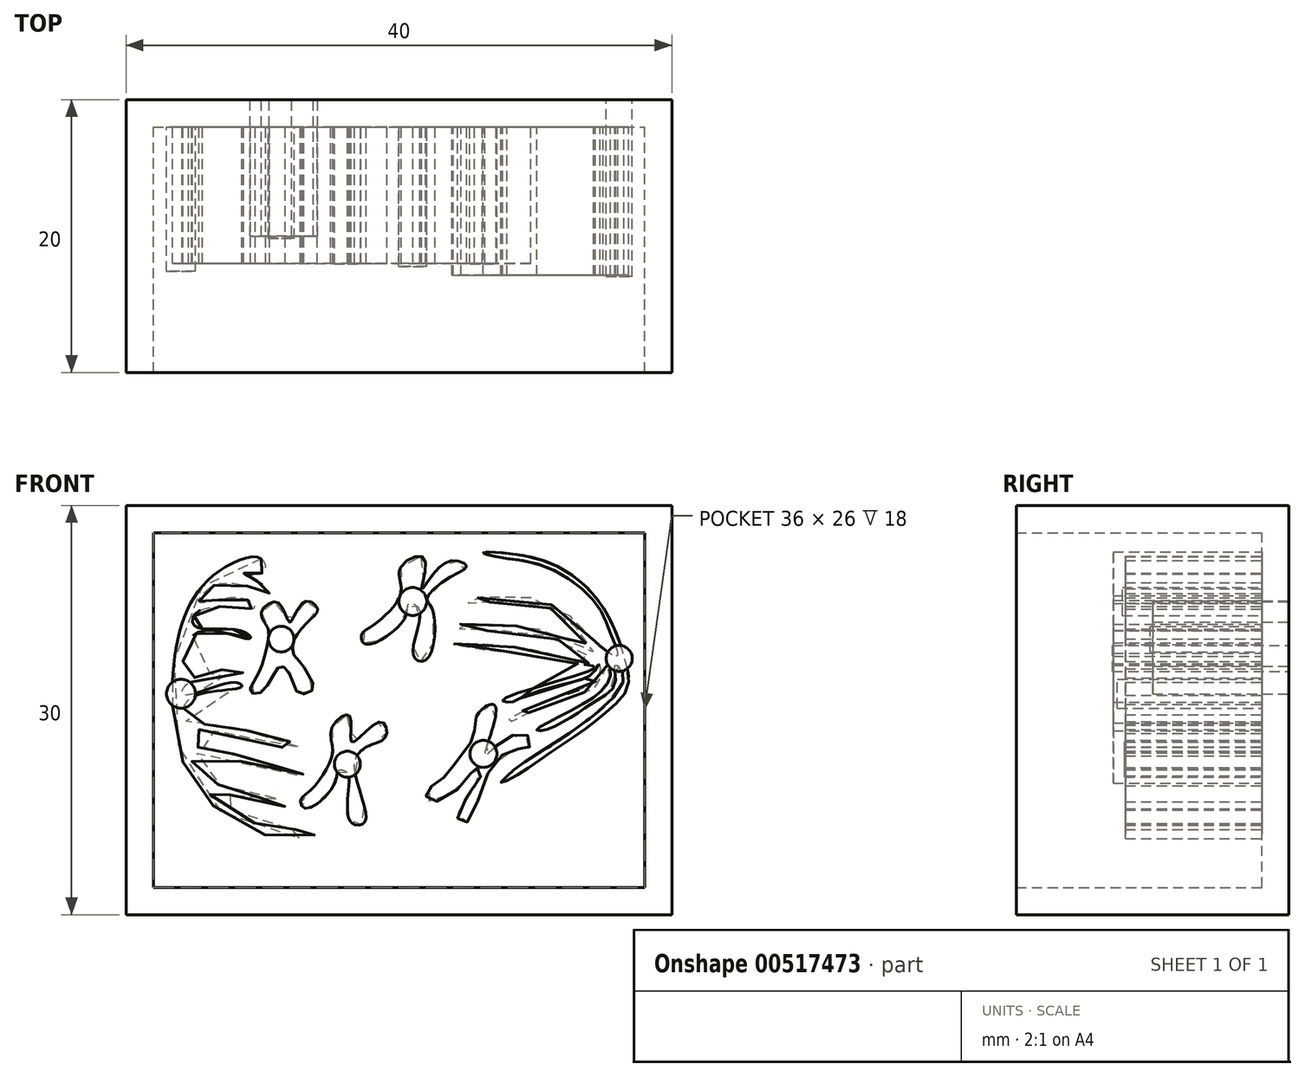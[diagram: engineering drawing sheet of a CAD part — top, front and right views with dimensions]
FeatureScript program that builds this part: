
annotation { "Feature Type Name" : "Feature", "Feature Type Description" : "" }
export const myFeature = defineFeature(function(context is Context, id is Id, definition is map)
    precondition{}
    {
        {
            var Q0;
            Q0=qCreatedBy(makeId("Front.planeOp"),FACE);
            var sketch = newSketch(context, id + "F0", { "sketchPlane" : qUnion([Q0])});
            skLineSegment(sketch, "E0.bottom", {"start": v(0, 0) * mm, "end": v(40, 0) * mm});
            skLineSegment(sketch, "E0.top", {"start": v(0, 30) * mm, "end": v(40, 30) * mm});
            skLineSegment(sketch, "E0.left", {"start": v(0, 0) * mm, "end": v(0, 30) * mm});
            skLineSegment(sketch, "E0.right", {"start": v(40, 0) * mm, "end": v(40, 30) * mm});
            skSolve(sketch);
        }
        {
            var Q0;
            Q0 = qSketchRegion(id + "F0", true);
            extrude(context, id + "F1", {"entities" : qUnion([Q0]), "depth" : 20 * mm, "offsetDistance" : 25 * mm});
        }
        {
            var Q0;
            Q0=makeQuery(id+"F1.opExtrude","CAP_FACE",FACE,{"disambiguationData":[OSD([sQuery(id+"F0.wireOp",EDGE,"E0.bottom"),sQuery(id+"F0.wireOp",EDGE,"E0.top"),sQuery(id+"F0.wireOp",EDGE,"E0.left"),sQuery(id+"F0.wireOp",EDGE,"E0.right")])],"isStart":false});
            shell(context, id + "F2", {"entities" : qUnion([Q0]), "thickness" : 2 * mm});
        }
        {
            var Q0;
            Q0=qCreatedBy(makeId("Front.planeOp"),FACE);
            var sketch = newSketch(context, id + "F3", { "sketchPlane" : qUnion([Q0])});
            skFitSpline(sketch, "E1", {"points": [v(9.93, 22.19) * mm, v(10.4, 20.93) * mm, v(10.3, 19.64) * mm, v(10.05, 18.55) * mm, v(9.52, 17.35) * mm, v(9.1, 16.41) * mm, v(9.73, 16.2) * mm, v(10.77, 17.52) * mm, v(11.37, 18.2) * mm, v(12.06, 17.5) * mm, v(12.66, 16.23) * mm, v(13.69, 16.52) * mm, v(13.32, 17.66) * mm, v(12.78, 18.46) * mm, v(12.14, 19.45) * mm, v(13.27, 21.42) * mm, v(14.04, 22.42) * mm, v(13.07, 22.95) * mm, v(11.98, 21.44) * mm, v(11.15, 22.87) * mm, v(9.93, 22.19) * mm]});
            skSolve(sketch);
        }
        {
            var Q0;
            Q0 = qSketchRegion(id + "F3", true);
            extrude(context, id + "F4", {"entities" : qUnion([Q0]), "depth" : 10 * mm, "offsetDistance" : 25 * mm});
        }
        {
            var Q0;
            Q0=makeQuery(id+"F2.opShell","OFFSET_FACE",FACE,{"disambiguationData":[OSD([sQuery(id+"F0.wireOp",EDGE,"E0.bottom"),sQuery(id+"F0.wireOp",EDGE,"E0.top"),sQuery(id+"F0.wireOp",EDGE,"E0.left"),sQuery(id+"F0.wireOp",EDGE,"E0.right")])]});
            var sketch = newSketch(context, id + "F5", { "sketchPlane" : qUnion([Q0])});
            skFitSpline(sketch, "E2", {"points": [v(15.1, 13.72) * mm, v(15.16, 12.14) * mm, v(14.66, 10.62) * mm, v(13.54, 9.13) * mm, v(12.78, 8.35) * mm, v(13.2, 7.78) * mm, v(15.3, 9.65) * mm, v(15.56, 10.57) * mm, v(16.2, 10.4) * mm, v(16.28, 8.97) * mm, v(16.23, 7.64) * mm, v(16.56, 6.7) * mm, v(17.53, 6.83) * mm, v(16.74, 10.92) * mm, v(17.86, 12.42) * mm, v(19.08, 13.14) * mm, v(18.62, 14.14) * mm, v(16.55, 12.66) * mm, v(16.38, 14.58) * mm, v(15.1, 13.72) * mm]});
            skSolve(sketch);
        }
        {
            var Q0;
            Q0 = qSketchRegion(id + "F5", true);
            extrude(context, id + "F6", {"entities" : qUnion([Q0]), "depth" : 10 * mm, "offsetDistance" : 25 * mm});
        }
        {
            var Q0;
            Q0=makeQuery(id+"F2.opShell","OFFSET_FACE",FACE,{"disambiguationData":[OSD([sQuery(id+"F0.wireOp",EDGE,"E0.bottom"),sQuery(id+"F0.wireOp",EDGE,"E0.top"),sQuery(id+"F0.wireOp",EDGE,"E0.left"),sQuery(id+"F0.wireOp",EDGE,"E0.right")])]});
            var sketch = newSketch(context, id + "F7", { "sketchPlane" : qUnion([Q0])});
            skFitSpline(sketch, "E3", {"points": [v(20.14, 25.5) * mm, v(20.17, 23.8) * mm, v(19.24, 22.18) * mm, v(17.97, 21.13) * mm, v(17.25, 20.52) * mm, v(17.49, 19.86) * mm, v(19.1, 20.42) * mm, v(20.57, 22.07) * mm, v(20.73, 22.8) * mm, v(21.4, 22.51) * mm, v(21.33, 20.84) * mm, v(21.16, 18.8) * mm, v(22.12, 18.8) * mm, v(22.4, 22.5) * mm, v(22.03, 23.13) * mm, v(23.72, 24.74) * mm, v(24.95, 25.56) * mm, v(24.15, 25.97) * mm, v(22.57, 25.06) * mm, v(21.67, 23.9) * mm, v(21.83, 26.14) * mm, v(20.14, 25.5) * mm]});
            skSolve(sketch);
        }
        {
            var Q0;
            Q0 = qSketchRegion(id + "F7", true);
            extrude(context, id + "F8", {"entities" : qUnion([Q0]), "depth" : 10 * mm, "offsetDistance" : 25 * mm});
        }
        {
            var Q0;
            Q0=makeQuery(id+"F2.opShell","OFFSET_FACE",FACE,{"disambiguationData":[OSD([sQuery(id+"F0.wireOp",EDGE,"E0.bottom"),sQuery(id+"F0.wireOp",EDGE,"E0.top"),sQuery(id+"F0.wireOp",EDGE,"E0.left"),sQuery(id+"F0.wireOp",EDGE,"E0.right")])]});
            var sketch = newSketch(context, id + "F9", { "sketchPlane" : qUnion([Q0])});
            skFitSpline(sketch, "E4", {"points": [v(25.65, 14.51) * mm, v(25.5, 13.18) * mm, v(24.93, 12.16) * mm, v(24.07, 11) * mm, v(22.97, 9.76) * mm, v(22.01, 9.02) * mm, v(22.4, 8.27) * mm, v(25.1, 10.05) * mm, v(25.53, 10.74) * mm, v(26.1, 10.5) * mm, v(24.3, 7.3) * mm, v(24.89, 6.71) * mm, v(26.77, 10.84) * mm, v(28.77, 12.15) * mm, v(29.6, 12.34) * mm, v(29.3, 13.23) * mm, v(27.1, 12.36) * mm, v(26.3, 11.67) * mm, v(27.02, 14.24) * mm, v(26.88, 15.42) * mm, v(25.65, 14.51) * mm]});
            skSolve(sketch);
        }
        {
            var Q0;
            Q0 = qSketchRegion(id + "F9", true);
            extrude(context, id + "F10", {"entities" : qUnion([Q0]), "depth" : 10 * mm, "offsetDistance" : 25 * mm});
        }
        {
            var Q0;
            Q0=makeQuery(id+"F2.opShell","OFFSET_FACE",FACE,{"disambiguationData":[OSD([sQuery(id+"F0.wireOp",EDGE,"E0.bottom"),sQuery(id+"F0.wireOp",EDGE,"E0.top"),sQuery(id+"F0.wireOp",EDGE,"E0.left"),sQuery(id+"F0.wireOp",EDGE,"E0.right")])]});
            var sketch = newSketch(context, id + "F11", { "sketchPlane" : qUnion([Q0])});
            skCircle(sketch, "E5", {"center": v(11.37, 20.2) * mm, "radius": 0.94 * mm});
            skPoint(sketch, "E5.first.point", {"position": v(10.43, 20.18) * mm});
            skPoint(sketch, "E5.second.point", {"position": v(12.15, 19.68) * mm});
            skPoint(sketch, "E5.third.point", {"position": v(10.45, 20.41) * mm});
            skSolve(sketch);
        }
        {
            var Q0;
            Q0 = qSketchRegion(id + "F11", true);
            extrude(context, id + "F12", {"entities" : qUnion([Q0]), "depth" : 8.18 * mm, "offsetDistance" : 25 * mm});
        }
        {
            var Q0;
            Q0=makeQuery(id+"F2.opShell","OFFSET_FACE",FACE,{"disambiguationData":[OSD([sQuery(id+"F0.wireOp",EDGE,"E0.bottom"),sQuery(id+"F0.wireOp",EDGE,"E0.top"),sQuery(id+"F0.wireOp",EDGE,"E0.left"),sQuery(id+"F0.wireOp",EDGE,"E0.right")])]});
            var sketch = newSketch(context, id + "F13", { "sketchPlane" : qUnion([Q0])});
            skCircle(sketch, "E6", {"center": v(21.01, 22.96) * mm, "radius": 1.02 * mm});
            skPoint(sketch, "E6.first.point", {"position": v(20.04, 23.28) * mm});
            skPoint(sketch, "E6.second.point", {"position": v(22.03, 23.1) * mm});
            skPoint(sketch, "E6.third.point", {"position": v(21.54, 22.08) * mm});
            skSolve(sketch);
        }
        {
            var Q0;
            Q0 = qSketchRegion(id + "F13", true);
            extrude(context, id + "F14", {"entities" : qUnion([Q0]), "depth" : 10.22 * mm, "offsetDistance" : 25 * mm});
        }
        {
            var Q0;
            Q0=makeQuery(id+"F2.opShell","OFFSET_FACE",FACE,{"disambiguationData":[OSD([sQuery(id+"F0.wireOp",EDGE,"E0.bottom"),sQuery(id+"F0.wireOp",EDGE,"E0.top"),sQuery(id+"F0.wireOp",EDGE,"E0.left"),sQuery(id+"F0.wireOp",EDGE,"E0.right")])]});
            var sketch = newSketch(context, id + "F15", { "sketchPlane" : qUnion([Q0])});
            skCircle(sketch, "E7", {"center": v(16.22, 11.03) * mm, "radius": 0.95 * mm});
            skPoint(sketch, "E7.first.point", {"position": v(15.44, 10.49) * mm});
            skPoint(sketch, "E7.second.point", {"position": v(17.11, 11.35) * mm});
            skPoint(sketch, "E7.third.point", {"position": v(16.02, 11.96) * mm});
            skSolve(sketch);
        }
        {
            var Q0;
            Q0 = qSketchRegion(id + "F15", true);
            extrude(context, id + "F16", {"entities" : qUnion([Q0]), "depth" : 10.05 * mm, "offsetDistance" : 25 * mm});
        }
        {
            var Q0;
            Q0=makeQuery(id+"F2.opShell","OFFSET_FACE",FACE,{"disambiguationData":[OSD([sQuery(id+"F0.wireOp",EDGE,"E0.bottom"),sQuery(id+"F0.wireOp",EDGE,"E0.top"),sQuery(id+"F0.wireOp",EDGE,"E0.left"),sQuery(id+"F0.wireOp",EDGE,"E0.right")])]});
            var sketch = newSketch(context, id + "F17", { "sketchPlane" : qUnion([Q0])});
            skCircle(sketch, "E8", {"center": v(26.19, 11.79) * mm, "radius": 1 * mm});
            skPoint(sketch, "E8.first.point", {"position": v(26.93, 11.14) * mm});
            skPoint(sketch, "E8.second.point", {"position": v(25.28, 12.2) * mm});
            skPoint(sketch, "E8.third.point", {"position": v(26.32, 12.77) * mm});
            skSolve(sketch);
        }
        {
            var Q0;
            Q0 = qSketchRegion(id + "F17", true);
            extrude(context, id + "F18", {"entities" : qUnion([Q0]), "depth" : 10.06 * mm, "offsetDistance" : 25 * mm});
        }
        {
            var Q0;
            Q0=makeQuery(id+"F2.opShell","OFFSET_FACE",FACE,{"disambiguationData":[OSD([sQuery(id+"F0.wireOp",EDGE,"E0.bottom"),sQuery(id+"F0.wireOp",EDGE,"E0.top"),sQuery(id+"F0.wireOp",EDGE,"E0.left"),sQuery(id+"F0.wireOp",EDGE,"E0.right")])]});
            var sketch = newSketch(context, id + "F19", { "sketchPlane" : qUnion([Q0])});
            skFitSpline(sketch, "E9", {"points": [v(34.36, 20.04) * mm, v(33.04, 21.45) * mm, v(30.56, 23) * mm, v(26.58, 23.33) * mm, v(24.56, 22.93) * mm, v(25.55, 22.83) * mm, v(28.34, 23.02) * mm, v(30.9, 22.55) * mm, v(32.6, 21.53) * mm, v(33.5, 20.14) * mm, v(34.26, 19.16) * mm, v(32.64, 19.96) * mm, v(31.15, 20.65) * mm, v(29.5, 21.05) * mm, v(27.42, 21.26) * mm, v(25.2, 21.29) * mm, v(23.89, 21.23) * mm, v(24.73, 20.9) * mm, v(27.63, 20.85) * mm, v(31.26, 20.32) * mm, v(34.08, 18.84) * mm, v(34.31, 18.43) * mm, v(31.53, 19.08) * mm, v(27.6, 19.7) * mm, v(24.73, 19.91) * mm, v(23.97, 19.81) * mm, v(25.12, 19.52) * mm, v(28.95, 19.21) * mm, v(32.82, 18.43) * mm, v(34.34, 18.06) * mm, v(27.6, 15.75) * mm, v(28.16, 15.58) * mm, v(28.75, 15.8) * mm, v(31.41, 16.73) * mm, v(34.26, 17.75) * mm, v(34.68, 18.38) * mm, v(34.64, 17.46) * mm, v(33.02, 16.43) * mm, v(28.24, 14.48) * mm, v(27.95, 14.05) * mm, v(28.7, 14.42) * mm, v(31.35, 15.53) * mm, v(33.37, 16.22) * mm, v(34.9, 17.13) * mm, v(35.01, 18.3) * mm, v(35.38, 18.27) * mm, v(35.34, 17.07) * mm, v(33.58, 15.5) * mm, v(30.52, 13.87) * mm, v(30.1, 13.53) * mm, v(30.58, 13.5) * mm, v(31.93, 14.08) * mm, v(33.4, 14.99) * mm, v(34.48, 15.7) * mm, v(35.83, 16.93) * mm, v(35.85, 18.26) * mm, v(36.3, 18.02) * mm, v(36.02, 16.29) * mm, v(29.2, 11.16) * mm, v(27.98, 10.23) * mm, v(27.47, 9.67) * mm, v(28.3, 10.03) * mm, v(30.04, 11.15) * mm, v(31.97, 12.48) * mm, v(33.84, 13.75) * mm, v(35.32, 14.98) * mm, v(36.71, 16.53) * mm, v(36.6, 18.57) * mm, v(35.21, 22.13) * mm, v(32.74, 24.85) * mm, v(29.08, 26.34) * mm, v(26.18, 26.53) * mm, v(27.23, 26.22) * mm, v(29.98, 25.75) * mm, v(33.16, 24.1) * mm, v(34.92, 22.05) * mm, v(35.65, 20.27) * mm, v(35.98, 18.96) * mm, v(34.36, 20.04) * mm]});
            skSolve(sketch);
        }
        {
            var Q0;
            Q0 = qSketchRegion(id + "F19", true);
            extrude(context, id + "F20", {"entities" : qUnion([Q0]), "depth" : 10.88 * mm, "offsetDistance" : 25 * mm});
        }
        {
            var Q0;
            Q0=makeQuery(id+"F2.opShell","OFFSET_FACE",FACE,{"disambiguationData":[OSD([sQuery(id+"F0.wireOp",EDGE,"E0.bottom"),sQuery(id+"F0.wireOp",EDGE,"E0.top"),sQuery(id+"F0.wireOp",EDGE,"E0.left"),sQuery(id+"F0.wireOp",EDGE,"E0.right")])]});
            var sketch = newSketch(context, id + "F21", { "sketchPlane" : qUnion([Q0])});
            skFitSpline(sketch, "E10", {"points": [v(9.92, 26.08) * mm, v(6.97, 25.3) * mm, v(4.36, 22.07) * mm, v(3.4, 16.86) * mm, v(4.08, 11.43) * mm, v(6.74, 7.7) * mm, v(11.81, 5.57) * mm, v(14, 6) * mm, v(13.23, 6.22) * mm, v(10.66, 6.32) * mm, v(7.42, 7.86) * mm, v(5.65, 9.43) * mm, v(11.42, 7.7) * mm, v(11.55, 8.28) * mm, v(9.81, 8.6) * mm, v(7.03, 9.44) * mm, v(5.3, 10.42) * mm, v(5, 11.78) * mm, v(12.7, 10.2) * mm, v(12.98, 10.48) * mm, v(11.4, 10.8) * mm, v(8.46, 11.6) * mm, v(5.78, 12.3) * mm, v(4.85, 12.4) * mm, v(4.83, 13.46) * mm, v(12.85, 12) * mm, v(12.32, 12.54) * mm, v(9.33, 13.36) * mm, v(6.38, 13.98) * mm, v(4.46, 14.1) * mm, v(4.66, 15.81) * mm, v(8.46, 16.7) * mm, v(7.87, 17.02) * mm, v(4.24, 16.13) * mm, v(4.65, 17.02) * mm, v(8.56, 17.65) * mm, v(7.44, 18.01) * mm, v(4.47, 17.52) * mm, v(5.24, 20.67) * mm, v(9.07, 20.23) * mm, v(8.55, 20.78) * mm, v(5, 21.18) * mm, v(5.64, 22.43) * mm, v(9.43, 22.49) * mm, v(8.33, 23.23) * mm, v(5.38, 22.9) * mm, v(6.97, 24.3) * mm, v(10.5, 23.56) * mm, v(9.67, 24.4) * mm, v(8.62, 25.02) * mm, v(10.03, 25.08) * mm, v(9.92, 26.08) * mm]});
            skSolve(sketch);
        }
        {
            var Q0;
            Q0 = qSketchRegion(id + "F21", true);
            extrude(context, id + "F22", {"entities" : qUnion([Q0]), "depth" : 10 * mm, "offsetDistance" : 25 * mm});
        }
        {
            var Q0;
            Q0=makeQuery(id+"F2.opShell","OFFSET_FACE",FACE,{"disambiguationData":[OSD([sQuery(id+"F0.wireOp",EDGE,"E0.bottom"),sQuery(id+"F0.wireOp",EDGE,"E0.top"),sQuery(id+"F0.wireOp",EDGE,"E0.left"),sQuery(id+"F0.wireOp",EDGE,"E0.right")])]});
            var sketch = newSketch(context, id + "F23", { "sketchPlane" : qUnion([Q0])});
            skSolve(sketch);
        }
        {
            var Q0;
            {var subQ0=sQuery(id+"F0.wireOp",EDGE,"E0.bottom");Q0=makeQuery(id+"F23.imprint","IMPRINT",FACE,{"disambiguationData":[TD([[makeQuery(id+"F23.imprint","IMPRINT",EDGE,{"derivedFrom":makeQuery(id+"F2.opShell","OFFSET_EDGE",EDGE,{"disambiguationData":[OSD([subQ0]),TDD([makeQuery(id+"F1.opExtrude","CAP_EDGE",EDGE,{"disambiguationData":[OSD([subQ0])],"isStart":true})])]})}),1.0]])]});}
            var sketch = newSketch(context, id + "F24", { "sketchPlane" : qUnion([Q0])});
            skCircle(sketch, "E11", {"center": v(4.03, 16.2) * mm, "radius": 1.06 * mm});
            skSolve(sketch);
        }
        {
            var Q0;
            Q0 = qSketchRegion(id + "F24", true);
            extrude(context, id + "F25", {"entities" : qUnion([Q0]), "depth" : 10.6 * mm, "offsetDistance" : 25 * mm});
        }
        {
            var Q0;
            Q0=qCreatedBy(makeId("Front.planeOp"),FACE);
            var sketch = newSketch(context, id + "F26", { "sketchPlane" : qUnion([Q0])});
            skCircle(sketch, "E12", {"center": v(36.14, 18.78) * mm, "radius": 0.96 * mm});
            skSolve(sketch);
        }
        {
            var Q0;
            Q0 = qSketchRegion(id + "F26", true);
            extrude(context, id + "F27", {"entities" : qUnion([Q0]), "depth" : 12.95 * mm, "offsetDistance" : 25 * mm});
        }
    });
